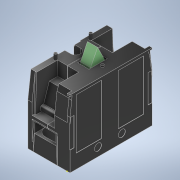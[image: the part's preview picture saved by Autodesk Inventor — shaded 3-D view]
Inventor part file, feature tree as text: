
AUTODESK INVENTOR PART (.ipt)
format: ipt  version: 2022 (Build 260153000, 153)  size: 3,118,592 bytes
history: native  units: mm
features: extrude x34, sketch x30, projected_geometry x12, chamfer x5, plane x3, emboss x1
ambient origin geometry x8: Origin, YZ Plane, XZ Plane, XY Plane, X Axis, Y Axis, Z Axis, Center Point
bodies: Solid1 (feature_tree)
feature tree (85):
  extrude  "Extrusion1"  Depth=2.0mm
  sketch  "Sketch2"  dims[d8=7.0mm d10=6.0mm]
  extrude  "Extrusion2"  Depth=6.0mm
  extrude  "Extrusion3"  Depth=1.0mm
  extrude  "Extrusion5"  Depth=3.0mm
  extrude  "Extrusion9"  Depth=10.5mm
  sketch  "Sketch6"  dims[d15=3.0mm d16=3.0mm]
  sketch  "Sketch8"  dims[d17=10.5mm d18=10.5mm]
  sketch  "Sketch9"  dims[d19=5.0mm d20=0.0mm d21=5.0mm d22=0.0mm]
  extrude  "Extrusion11"  Depth=5.0mm TaperAngle=0.0deg
  extrude  "Extrusion14"  Depth=3.0mm
  sketch  "Sketch12"  dims[d27=2.0mm d29=0.3mm]
  extrude  "Extrusion15"  Depth=2.0mm
  extrude  "Extrusion16"  Depth=4.0mm
  sketch  "Sketch13"  dims[d30=4.0mm d31=4.0mm]
  extrude  "Extrusion17"  Depth=1.0mm
  extrude  "Extrusion18"  Depth=2.0mm TaperAngle=0.0deg
  extrude  "Extrusion19"  Depth=1.0mm
  extrude  "Extrusion20"  Depth=6.5mm
  plane  "Work Plane1"
  sketch  "Sketch16"  dims[d57=6.0mm d58=1.0mm]
  extrude  "Extrusion21"  Depth=1.0mm
  extrude  "Extrusion22"  Depth=4.5mm
  extrude  "Extrusion23"  Depth=5.0mm
  plane  "Work Plane2"
  sketch  "Sketch18"  dims[d61=6.5mm d62=1.0mm]
  extrude  "Extrusion24"  Depth=4.5mm
  extrude  "Extrusion25"  Depth=4.5mm
  chamfer  "Chamfer2"  Distance=6.0mm
  chamfer  "Chamfer3"  Angle=45.0deg  [1 undecoded]
  extrude  "Extrusion26"  TaperAngle=45.0deg  [1 undecoded]
  extrude  "Extrusion27"  Depth=3.7mm TaperAngle=0.0deg
  extrude  "Extrusion28"  Depth=3.0mm
  extrude  "Extrusion29"  Depth=0.5mm
  extrude  "Extrusion30"  Depth=2.4mm
  extrude  "Extrusion31"  TaperAngle=0.0deg  [1 undecoded]
  chamfer  "Chamfer4"  Distance=4.0mm
  extrude  "Extrusion32"  TaperAngle=0.0deg  [1 undecoded]
  extrude  "Extrusion33"  Depth=1.0mm
  sketch  "Sketch25"  dims[d75=3.35mm]
  extrude  "Extrusion34"  Depth=18.0mm
  extrude  "Extrusion35"  Depth=9.0mm
  extrude  "Extrusion36"  Depth=3.0mm
  sketch  "Sketch27"  dims[d77=4.0mm]
  extrude  "Extrusion37"  Depth=9.0mm
  extrude  "Extrusion38"  Depth=6.0mm
  extrude  "Extrusion39"  Depth=2.0mm
  emboss  "Emboss1"
  plane  "Work Plane4"
  extrude  "Extrusion40"  Depth=10.0mm
  sketch  "Sketch33"  dims[d92=3.0mm]
  chamfer  "Chamfer5"  Distance=0.1mm
  chamfer  "Chamfer6"  Distance=0.09mm
  extrude  "Extrusion41"  Depth=2.5mm
  sketch  "Sketch1"  dims[d5=15.0mm d6=0.0mm d7=2.0mm]
  projected_geometry  "Projected Loop1"
  sketch  "Sketch4"  dims[d11=6.0mm d14=1.0mm]
  sketch  "Sketch11"  dims[d25=3.5mm d26=3.0mm]
  sketch  "Sketch14"  dims[d32=0.5mm d33=0.0mm d42=1.0mm]
  sketch  "Sketch15"  dims[d43=1.0mm d45=2.0mm d46=0.0mm]
  sketch  "Sketch17"  dims[d59=6.5mm d60=14.2mm]
  projected_geometry  "Projected Loop2"
  projected_geometry  "Projected Loop3"
  projected_geometry  "Projected Loop4"
  sketch  "Sketch19"  dims[d64=6.0mm d66=4.5mm]
  sketch  "Sketch20"  dims[d67=5.5mm d68=5.0mm]
  projected_geometry  "Projected Loop5"
  sketch  "Sketch21"  dims[d69=5.0mm d70=4.5mm]
  sketch  "Sketch22"  dims[d71=5.5mm d72=4.5mm]
  projected_geometry  "Projected Loop6"
  projected_geometry  "Projected Loop7"
  projected_geometry  "Projected Loop8"
  sketch  "Sketch23"  dims[d73=0.1mm]
  sketch  "Sketch24"  dims[d74=3.35mm]
  projected_geometry  "Projected Loop9"
  projected_geometry  "Projected Loop10"
  projected_geometry  "Projected Loop11"
  sketch  "Sketch26"  dims[d76=4.5mm]
  sketch  "Sketch28"  dims[d78=6.5mm]
  sketch  "Sketch29"  dims[d79=4.0mm d80=6.0mm d81=0.0mm]
  sketch  "Sketch30"  dims[d88=3.5mm]
  sketch  "Sketch31"  dims[d89=3.5mm]
  sketch  "Sketch32"  dims[d90=6.0mm]
  sketch  "Sketch34"  dims[d93=0.2mm d94=45.0deg d95=45.0deg d96=3.7mm d97=0.0mm d99=3.0mm d100=0.5mm d101=2.4mm d102=0.0mm d103=4.0mm d104=0.0mm d105=0.0mm d106=0.0mm d110=1.0mm d111=18.0mm d112=9.0mm d113=3.0mm d114=9.0mm d115=6.0mm d116=2.0mm d117=10.0mm d118=0.1mm d119=0.0mm d120=0.09mm d121=0.0mm d122=2.5mm d123=2.5mm d125=2.0mm d126=2.0mm d127=0.09mm d128=0.0mm d130=0.0mm d131=1.173362mm d132=0.5mm d133=1.0mm d134=0.0mm d135=-13.0mm d136=5.5mm d137=3.0mm d138=8.0mm d139=3.0mm d140=18.850282mm d141=2.0mm d142=10.0mm d143=5.0mm d144=0.0mm d145=5.0mm d146=0.0mm d147=10.0mm d148=0.0mm d149=-3.5mm d150=2.0mm d151=3.5mm d152=10.0mm d153=0.0mm d154=0.7mm d155=10.0mm d156=0.0mm d157=0.9mm d158=0.5mm d159=45.0deg d160=0.5mm d161=0.5mm d162=45.0deg d163=0.08mm d164=0.0mm d166=0.08mm d167=0.08mm d168=10.0mm d169=0.0mm d170=5.0mm d171=0.0mm d172=5.0mm d173=0.0mm d174=56.0mm d175=0.0mm d176=10.0mm d177=0.0mm d178=0.8mm d179=10.0mm d180=0.0mm d181=0.5mm d182=0.5mm d183=45.0deg d184=0.5mm d185=0.0mm d186=0.1mm d187=0.1mm d189=90.0deg d190=3.0mm d191=0.1mm d192=0.1mm d194=0.1mm d196=4.4mm d197=1.25mm d198=6.0mm d199=0.1mm d200=3.75mm d201=14.0mm d202=4.4mm d203=0.35mm d204=0.5mm d205=0.0mm d206=2.0mm d207=3.0mm d208=0.5mm d209=0.0mm d210=0.5mm d211=0.0mm d212=2.0mm d213=2.0mm d214=0.0mm d215=0.0mm d216=0.5mm d217=0.0mm d218=5.0mm d219=0.0mm d220=5.0mm d221=0.0mm d222=1.0mm d223=1.5mm d224=0.5mm d225=0.0mm d226=0.1mm d227=0.1mm d228=0.2mm d229=0.0mm d231=-1.0mm d233=5.0mm d234=5.0mm d237=0.0mm d238=6.5mm d239=0.75mm d240=3.6mm d241=0.0mm d242=2.0mm d243=0.5mm d244=45.0deg d245=2.0mm d246=0.5mm d247=45.0deg d249=3.6mm d250=0.0mm d251=6.25mm d252=6.25mm d253=14.6mm d254=14.6mm d38=0.5mm d39=0.872665mm d40=0.5mm d41=0.872665mm]
  projected_geometry  "Projected Loop12"
note: 4 required parameter values undecoded (feature->parameter linkage not recoverable at this tier; creation-order binding heuristic only, values carry confidence <= 0.55)
